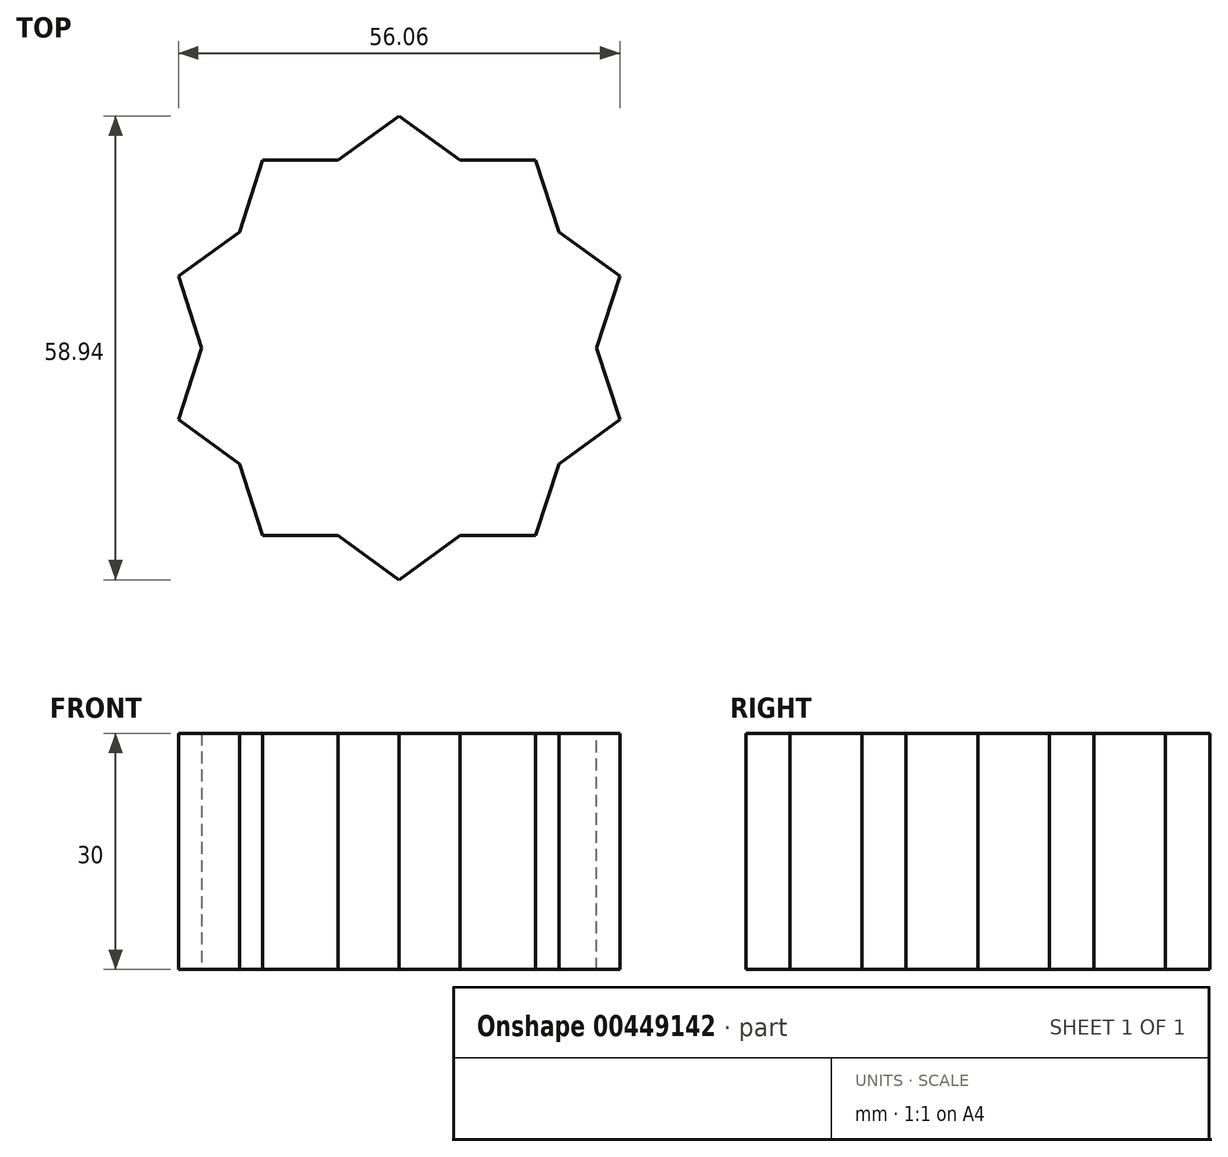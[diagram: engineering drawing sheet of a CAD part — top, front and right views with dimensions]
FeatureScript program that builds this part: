
annotation { "Feature Type Name" : "Feature", "Feature Type Description" : "" }
export const myFeature = defineFeature(function(context is Context, id is Id, definition is map)
    precondition{}
    {
        {
            var Q0;
            Q0=qCreatedBy(makeId("Top.planeOp"),FACE);
            cPlane(context, id + "F0", {"entities" : qUnion([Q0]), "cplaneType" : CPlaneType.OFFSET, "offset" : 15 * mm, "width" : 150 * mm, "height" : 150 * mm});
        }
        {
            var Q0;
            Q0=qCreatedBy(id+"F0.planeOp",FACE);
            var sketch = newSketch(context, id + "F1", { "sketchPlane" : qUnion([Q0])});
            skCircle(sketch, "E0.cCircle", {"center": v(0, 0) * mm, "radius": 23.84 * mm, "construction": true});
            skLineSegment(sketch, "E0.0", {"start": v(-17.32, 23.84) * mm, "end": v(17.32, 23.84) * mm});
            skLineSegment(sketch, "E0.1", {"start": v(17.32, 23.84) * mm, "end": v(28.03, -9.1) * mm});
            skLineSegment(sketch, "E0.2", {"start": v(28.03, -9.1) * mm, "end": v(0, -29.47) * mm});
            skLineSegment(sketch, "E0.3", {"start": v(0, -29.47) * mm, "end": v(-28.03, -9.1) * mm});
            skLineSegment(sketch, "E0.4", {"start": v(-28.03, -9.1) * mm, "end": v(-17.32, 23.84) * mm});
            skPoint(sketch, "E0.0.midPoint", {"position": v(0, 23.84) * mm});
            skSolve(sketch);
        }
        {
            var Q0;
            Q0=qCreatedBy(makeId("Top.planeOp"),FACE);
            cPlane(context, id + "F2", {"entities" : qUnion([Q0]), "cplaneType" : CPlaneType.OFFSET, "offset" : 15 * mm, "oppositeDirection" : true, "width" : 150 * mm, "height" : 150 * mm});
        }
        {
            var Q0;
            Q0=qCreatedBy(id+"F2.planeOp",FACE);
            var sketch = newSketch(context, id + "F3", { "sketchPlane" : qUnion([Q0])});
            skCircle(sketch, "E1.cCircle", {"center": v(0, 0) * mm, "radius": 23.84 * mm, "construction": true});
            skLineSegment(sketch, "E1.0", {"start": v(17.32, -23.84) * mm, "end": v(-17.32, -23.84) * mm});
            skLineSegment(sketch, "E1.1", {"start": v(-17.32, -23.84) * mm, "end": v(-28.03, 9.1) * mm});
            skLineSegment(sketch, "E1.2", {"start": v(-28.03, 9.1) * mm, "end": v(0, 29.47) * mm});
            skLineSegment(sketch, "E1.3", {"start": v(0, 29.47) * mm, "end": v(28.03, 9.1) * mm});
            skLineSegment(sketch, "E1.4", {"start": v(28.03, 9.1) * mm, "end": v(17.32, -23.84) * mm});
            skPoint(sketch, "E1.0.midPoint", {"position": v(0, -23.84) * mm});
            skSolve(sketch);
        }
        {
            var Q0;
            Q0=qCreatedBy(makeId("Right.planeOp"),FACE);
            cPlane(context, id + "F4", {"entities" : qUnion([Q0]), "cplaneType" : CPlaneType.OFFSET, "offset" : (28.02 / 2) * mm, "width" : 150 * mm, "height" : 150 * mm});
        }
        {
            var Q0;
            Q0=makeQuery(id+"F1.imprint","IMPRINT",FACE,{"disambiguationData":[TD([[makeQuery(id+"F1.imprint","IMPRINT",EDGE,{"derivedFrom":sQuery(id+"F1.wireOp",EDGE,"E0.0")}),-1.0]])]});
            extrude(context, id + "F5", {"entities" : qUnion([Q0]), "oppositeDirection" : true, "depth" : 30 * mm});
        }
        {
            var Q0;
            Q0=makeQuery(id+"F3.imprint","IMPRINT",FACE,{"disambiguationData":[TD([[makeQuery(id+"F3.imprint","IMPRINT",EDGE,{"derivedFrom":sQuery(id+"F3.wireOp",EDGE,"E1.0")}),-1.0]])]});
            extrude(context, id + "F6", {"entities" : qUnion([Q0]), "operationType" : NewBodyOperationType.ADD, "depth" : 30 * mm});
        }
    });
